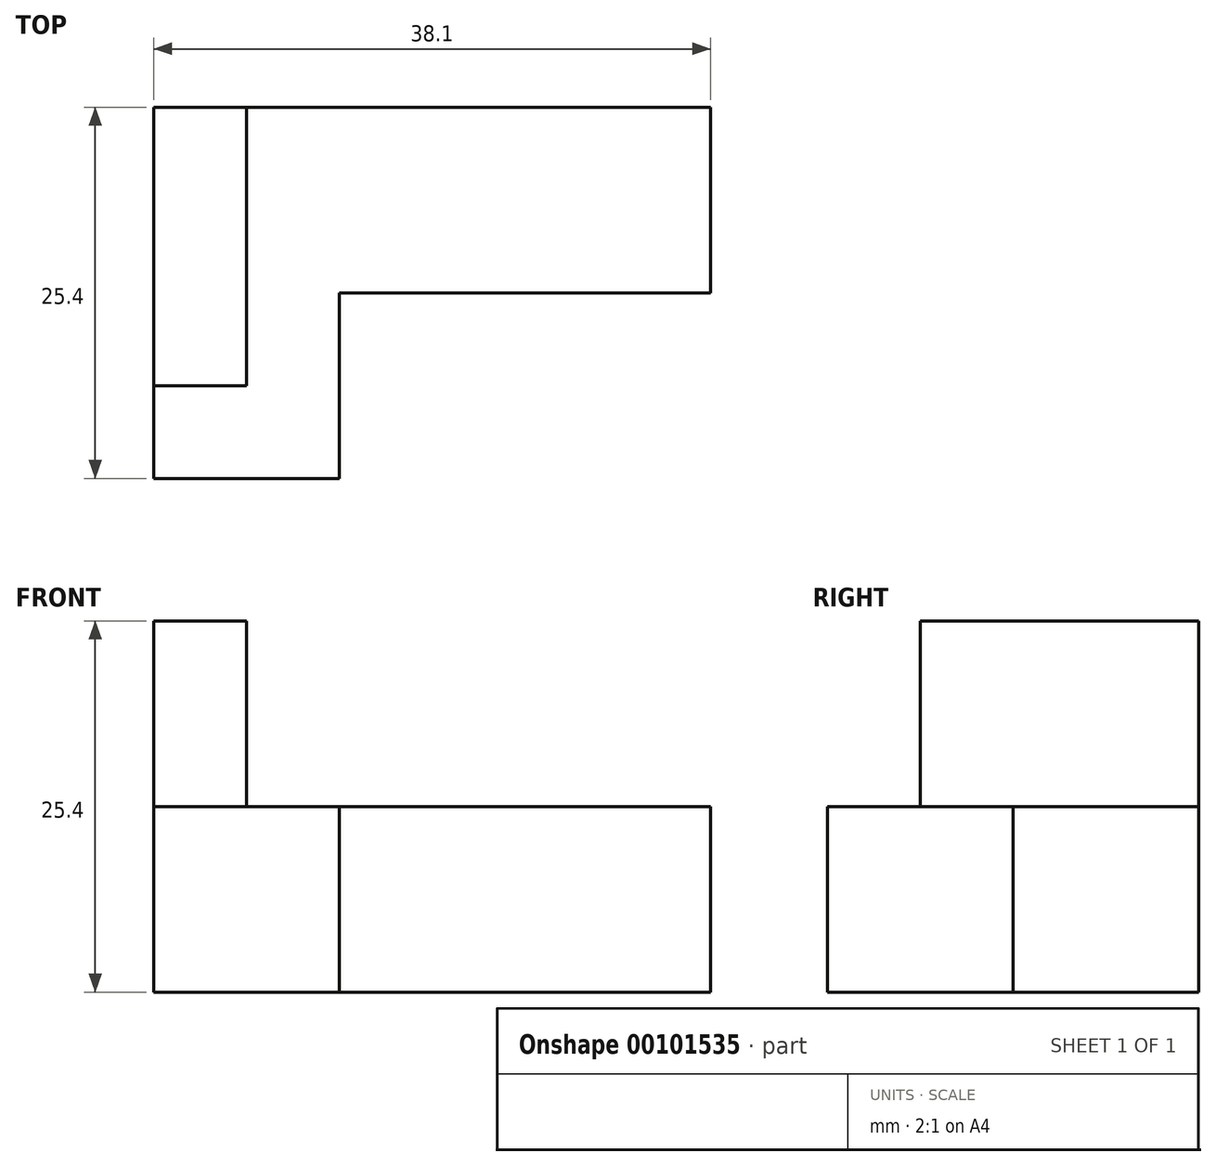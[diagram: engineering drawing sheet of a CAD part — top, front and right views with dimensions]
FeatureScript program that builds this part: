
annotation { "Feature Type Name" : "Feature", "Feature Type Description" : "" }
export const myFeature = defineFeature(function(context is Context, id is Id, definition is map)
    precondition{}
    {
        {
            var Q0;
            Q0=qCreatedBy(makeId("Top.planeOp"),FACE);
            var sketch = newSketch(context, id + "F0", { "sketchPlane" : qUnion([Q0])});
            skLineSegment(sketch, "E0", {"start": v(0, 25.4) * mm, "end": v(38.1, 25.4) * mm});
            skLineSegment(sketch, "E1", {"start": v(38.1, 25.4) * mm, "end": v(38.1, 12.7) * mm});
            skLineSegment(sketch, "E2", {"start": v(38.1, 12.7) * mm, "end": v(12.7, 12.7) * mm});
            skLineSegment(sketch, "E3", {"start": v(12.7, 12.7) * mm, "end": v(12.7, 0) * mm});
            skLineSegment(sketch, "E4", {"start": v(12.7, 0) * mm, "end": v(0, 0) * mm});
            skLineSegment(sketch, "E5", {"start": v(0, 0) * mm, "end": v(0, 25.4) * mm});
            skSolve(sketch);
        }
        {
            var Q0;
            Q0=makeQuery(id+"F0.imprint","IMPRINT",FACE,{"disambiguationData":[TD([[makeQuery(id+"F0.imprint","IMPRINT",EDGE,{"derivedFrom":sQuery(id+"F0.wireOp",EDGE,"E0")}),-1.0]])]});
            extrude(context, id + "F1", {"entities" : qUnion([Q0]), "depth" : 12.7 * mm});
        }
        {
            var Q0;
            Q0=makeQuery(id+"F1.opExtrude","SWEPT_FACE",FACE,{"disambiguationData":[OSD([sQuery(id+"F0.wireOp",EDGE,"E5")])]});
            var sketch = newSketch(context, id + "F2", { "sketchPlane" : qUnion([Q0])});
            skLineSegment(sketch, "E6.bottom", {"start": v(-25.4, 0) * mm, "end": v(-6.35, 0) * mm});
            skLineSegment(sketch, "E6.top", {"start": v(-25.4, 25.4) * mm, "end": v(-6.35, 25.4) * mm});
            skLineSegment(sketch, "E6.left", {"start": v(-25.4, 0) * mm, "end": v(-25.4, 25.4) * mm});
            skLineSegment(sketch, "E6.right", {"start": v(-6.35, 0) * mm, "end": v(-6.35, 25.4) * mm});
            skSolve(sketch);
        }
        {
            var Q0;
            {var subQ0=sQuery(id+"F2.wireOp",EDGE,"E6.top");Q0=makeQuery(id+"F2.imprint","IMPRINT",FACE,{"disambiguationData":[TD([[makeQuery(id+"F2.imprint","IMPRINT",EDGE,{"derivedFrom":subQ0}),-1.0]])]});}
            extrude(context, id + "F3", {"entities" : qUnion([Q0]), "operationType" : NewBodyOperationType.ADD, "oppositeDirection" : true, "depth" : 6.35 * mm});
        }
    });
